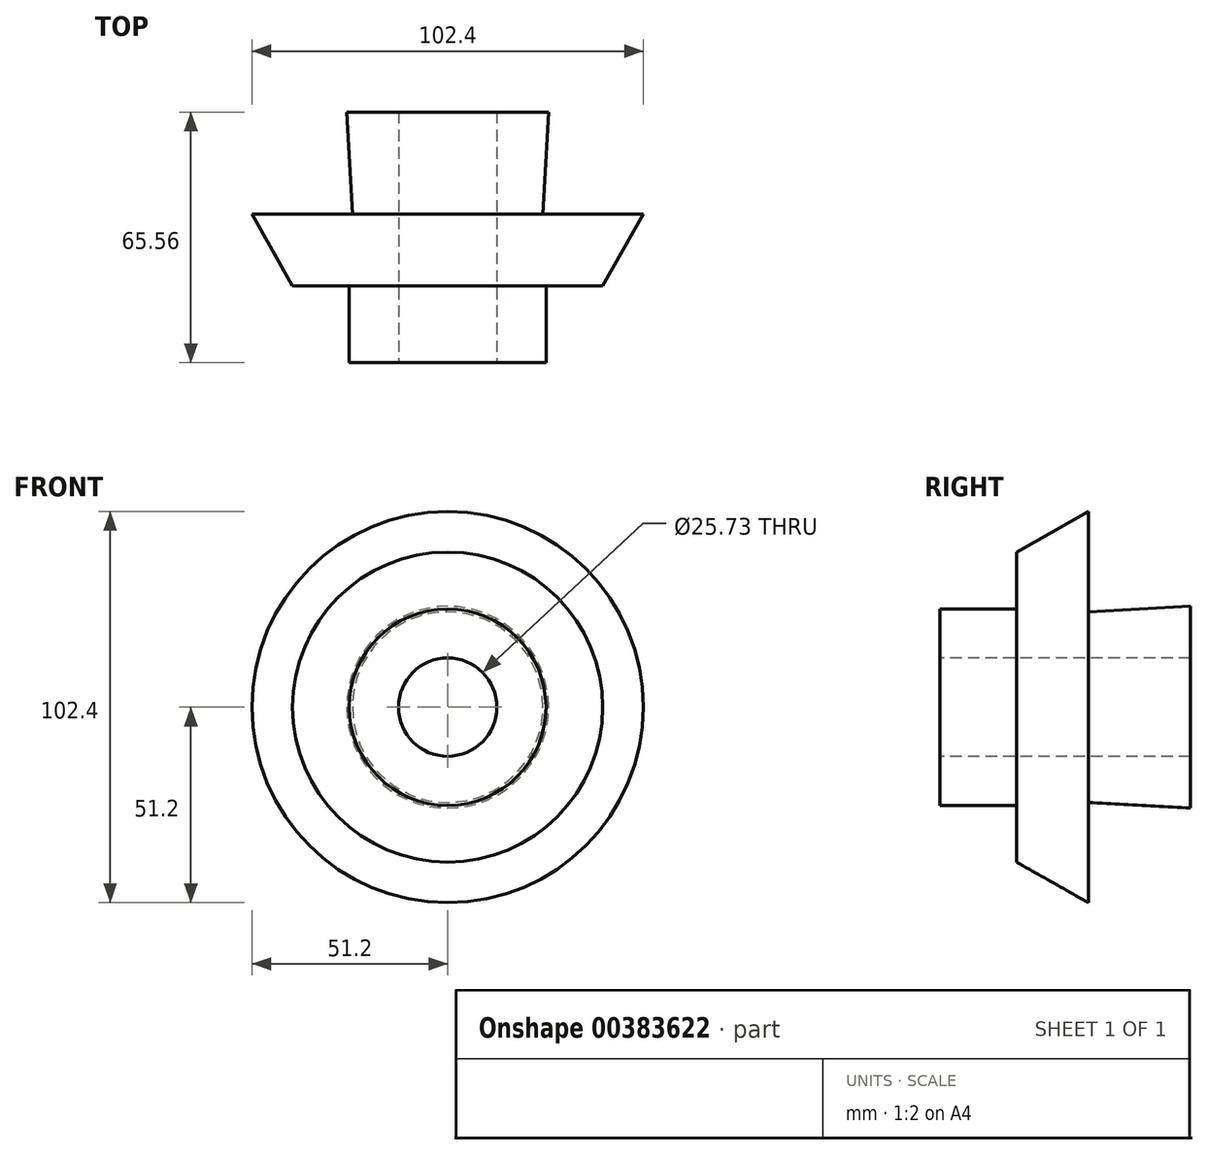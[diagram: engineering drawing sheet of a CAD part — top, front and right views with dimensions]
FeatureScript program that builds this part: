
annotation { "Feature Type Name" : "Feature", "Feature Type Description" : "" }
export const myFeature = defineFeature(function(context is Context, id is Id, definition is map)
    precondition{}
    {
        {
            var Q0;
            Q0=qCreatedBy(makeId("Right.planeOp"),FACE);
            var sketch = newSketch(context, id + "F0", { "sketchPlane" : qUnion([Q0])});
            skLineSegment(sketch, "E0", {"start": v(-38.9, 12.87) * mm, "end": v(-38.9, 25.73) * mm});
            skLineSegment(sketch, "E1", {"start": v(-38.9, 25.73) * mm, "end": v(-18.7, 25.73) * mm});
            skLineSegment(sketch, "E2", {"start": v(-18.7, 25.73) * mm, "end": v(-18.82, 40.57) * mm});
            skLineSegment(sketch, "E3", {"start": v(-18.82, 40.57) * mm, "end": v(0, 51.2) * mm});
            skLineSegment(sketch, "E4", {"start": v(0, 51.2) * mm, "end": v(0, 24.93) * mm});
            skLineSegment(sketch, "E5", {"start": v(0, 24.93) * mm, "end": v(26.65, 26.4) * mm});
            skLineSegment(sketch, "E6", {"start": v(26.65, 26.4) * mm, "end": v(26.65, 12.87) * mm});
            skLineSegment(sketch, "E7", {"start": v(26.65, 12.87) * mm, "end": v(-38.9, 12.87) * mm});
            skLineSegment(sketch, "E8", {"start": v(-65.7, 0) * mm, "end": v(49.3, 0) * mm, "construction": true});
            skSolve(sketch);
        }
        {
            var Q0;
            Q0 = qSketchRegion(id + "F0", true);
            var Q1;
            Q1=sQuery(id+"F0.wireOp",EDGE,"E8");
            revolve(context, id + "F1", {"entities" : qUnion([Q0]), "axis" : qUnion([Q1]), "revolveType" : RevolveType.FULL});
        }
    });
